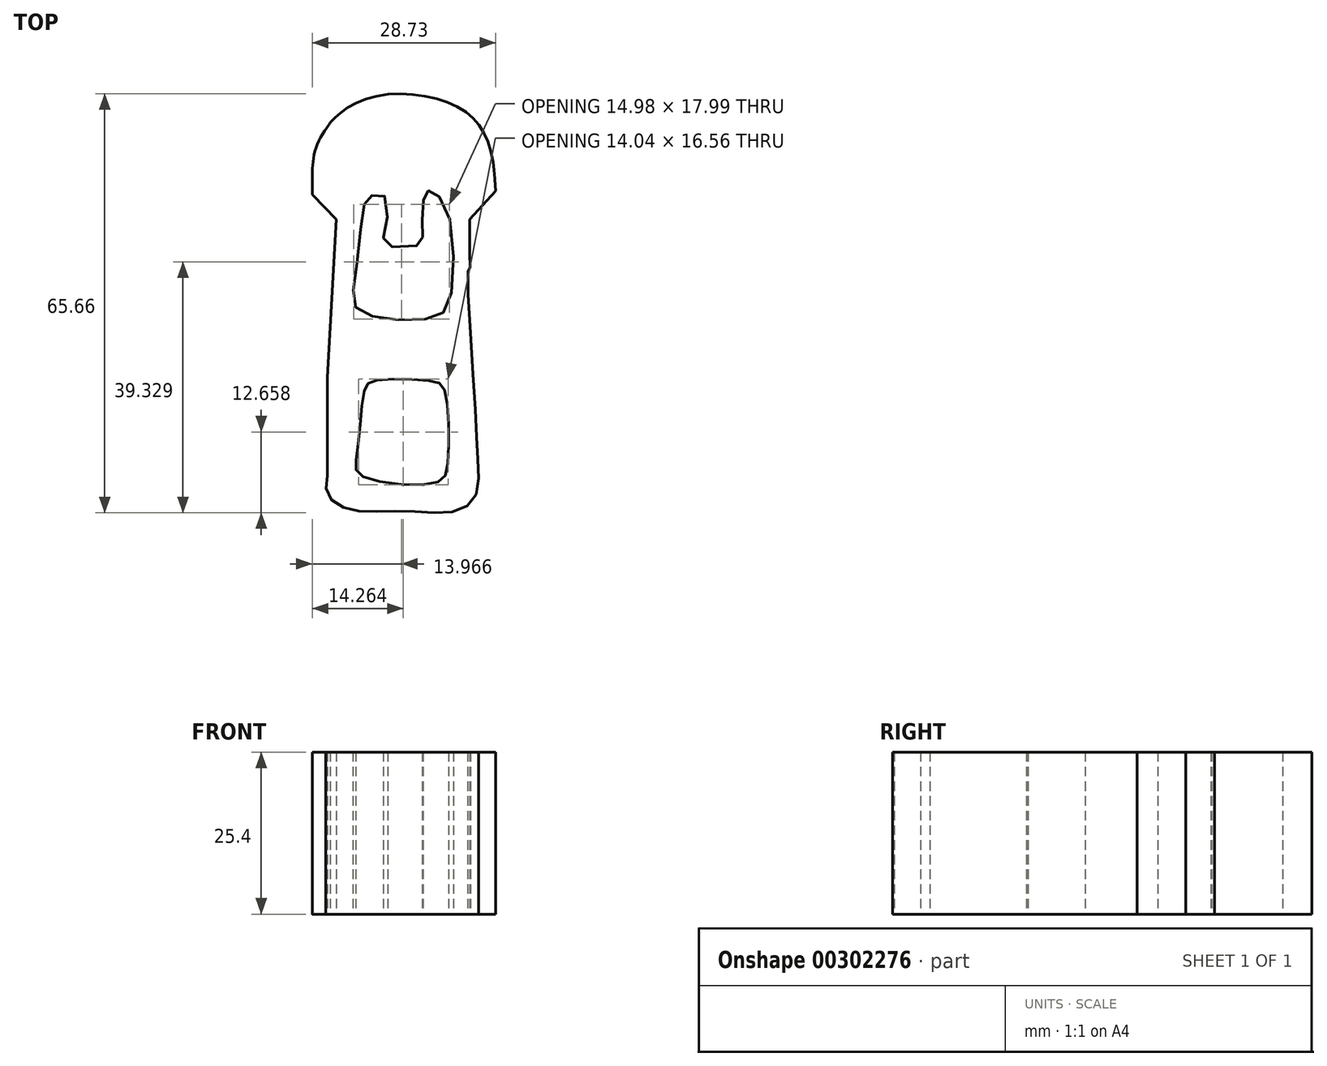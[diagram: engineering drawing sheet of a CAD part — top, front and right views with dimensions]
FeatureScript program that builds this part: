
annotation { "Feature Type Name" : "Feature", "Feature Type Description" : "" }
export const myFeature = defineFeature(function(context is Context, id is Id, definition is map)
    precondition{}
    {
        {
            var Q0;
            Q0=qCreatedBy(makeId("Top.planeOp"),FACE);
            var sketch = newSketch(context, id + "F0", { "sketchPlane" : qUnion([Q0])});
            skLineSegment(sketch, "E0", {"start": v(0, 0) * mm, "end": v(-3.75, 3.9) * mm});
            skFitSpline(sketch, "E1", {"points": [v(-3.75, 3.9) * mm, v(-3.75, 7.8) * mm, v(-2.83, 12.2) * mm, v(-0.98, 15.18) * mm, v(-0.98, 15.28) * mm, v(-1.09, 15.18) * mm], "startDerivative": vector(-0.27, 12.98) * mm, "endDerivative": vector(-2.13, -2.7) * mm});
            skFitSpline(sketch, "E2", {"points": [v(-0.98, 15.18) * mm, v(1.18, 17.16) * mm, v(6.25, 19.33) * mm, v(13.94, 19.33) * mm, v(20.02, 17.01) * mm, v(23.07, 13.68) * mm, v(24.66, 8.17) * mm, v(24.95, 4.4) * mm, v(24.95, 4.55) * mm], "startDerivative": vector(17.8, 19) * mm, "endDerivative": vector(-0.1, 9.42) * mm});
            skLineSegment(sketch, "E3", {"start": v(24.95, 4.48) * mm, "end": v(20.9, 0) * mm});
            skLineSegment(sketch, "E4", {"start": v(0, 0) * mm, "end": v(-1.43, -24.73) * mm});
            skLineSegment(sketch, "E5", {"start": v(-1.43, -24.73) * mm, "end": v(-1.43, -40.1) * mm});
            skFitSpline(sketch, "E6", {"points": [v(-1.43, -40.1) * mm, v(-1.43, -42.99) * mm, v(1.18, -45.16) * mm, v(5.82, -45.74) * mm, v(12.34, -45.74) * mm, v(18.43, -45.74) * mm, v(21.76, -43.42) * mm, v(22.2, -38.35) * mm, v(21.47, -25.3) * mm, v(20.75, -7.62) * mm, v(20.9, -7.62) * mm, v(20.9, -5.02) * mm, v(20.9, 0) * mm], "startDerivative": vector(-8.75, -48.28) * mm, "endDerivative": vector(1.42, 59.6) * mm});
            skFitSpline(sketch, "E7", {"points": [v(4.37, -26.9) * mm, v(3.21, -37.05) * mm, v(3.79, -40.1) * mm, v(15.53, -41.25) * mm, v(17.41, -38.35) * mm, v(16.98, -26.9) * mm, v(14.95, -25.3) * mm, v(5.82, -25.3) * mm, v(4.37, -26.9) * mm]});
            skPoint(sketch, "E8.5.internal.snap0", {"position": v(-0.71, -12.36) * mm});
            skFitSpline(sketch, "E8", {"points": [v(4.37, 2.38) * mm, v(3.07, -8.2) * mm, v(2.92, -13.57) * mm, v(7.27, -15.45) * mm, v(15.39, -15.3) * mm, v(17.85, -12.36) * mm, v(17.12, 2.09) * mm, v(14.8, 4.4) * mm, v(14.08, 4.4) * mm, v(13.5, 1.22) * mm, v(13.5, -2.7) * mm, v(13.21, -3.86) * mm, v(7.7, -4) * mm, v(7.7, -1.54) * mm, v(7.41, 3.83) * mm, v(5.38, 3.68) * mm, v(4.37, 2.38) * mm]});
            skFitSpline(sketch, "E9", {"points": [v(0, 0) * mm, v(-0.17, -2.98) * mm], "startDerivative": vector(-0.17, -2.98) * mm, "endDerivative": vector(-0.17, -2.98) * mm});
            skSolve(sketch);
        }
        {
            var Q0;
            Q0 = qSketchRegion(id + "F0", true);
            extrude(context, id + "F1", {"entities" : qUnion([Q0]), "depth" : 25.4 * mm});
        }
    });
